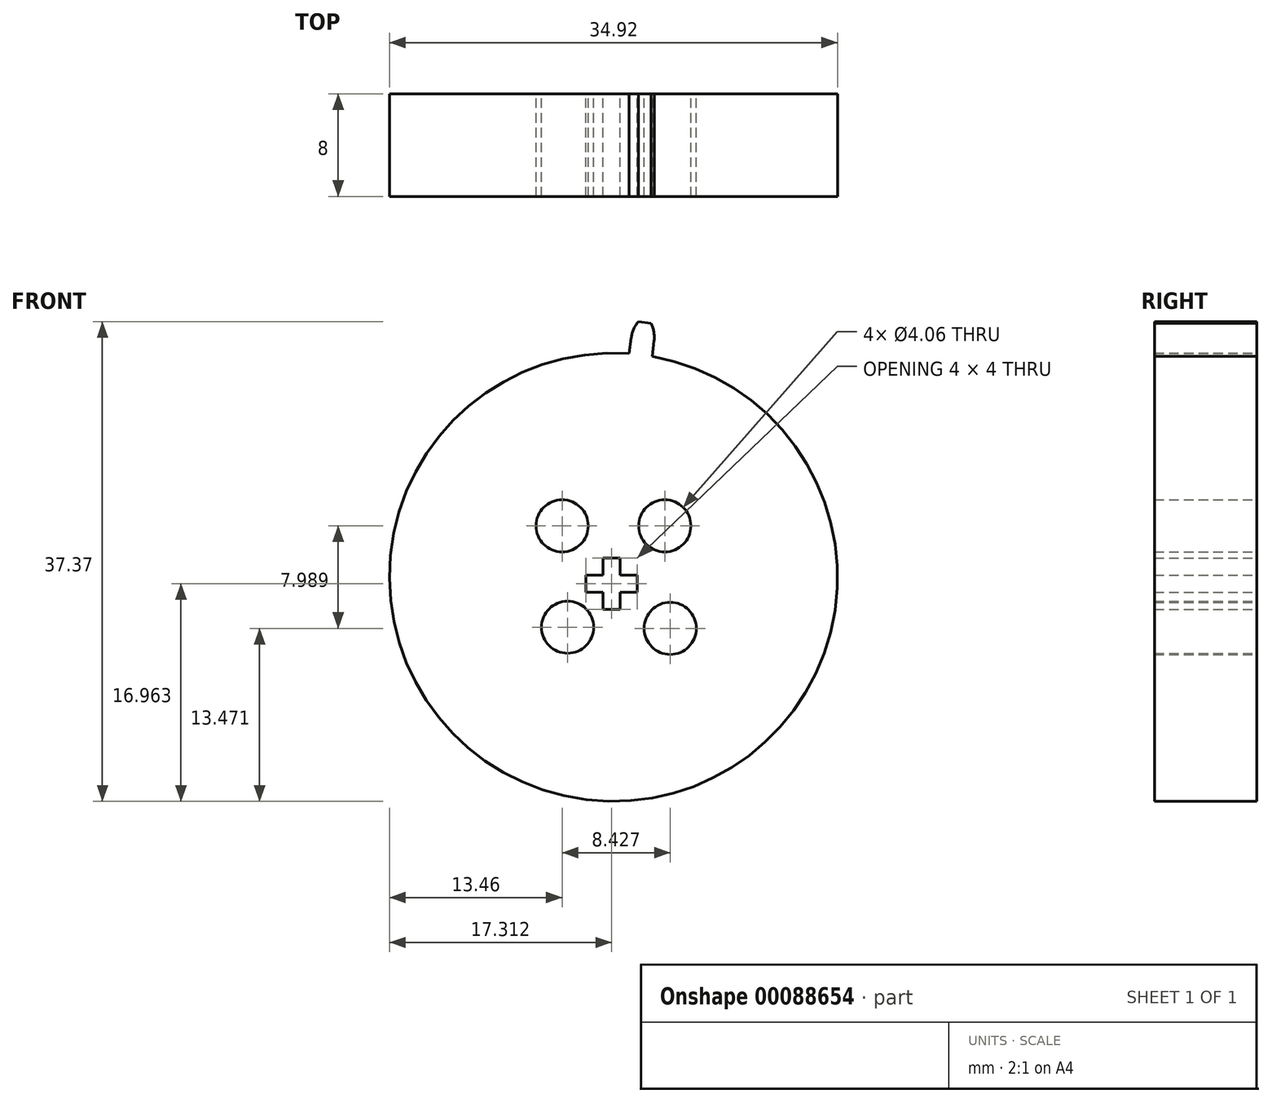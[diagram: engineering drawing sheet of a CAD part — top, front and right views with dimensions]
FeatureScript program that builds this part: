
annotation { "Feature Type Name" : "Feature", "Feature Type Description" : "" }
export const myFeature = defineFeature(function(context is Context, id is Id, definition is map)
    precondition{}
    {
        {
            var Q0;
            Q0=qCreatedBy(makeId("Front.planeOp"),FACE);
            var sketch = newSketch(context, id + "F0", { "sketchPlane" : qUnion([Q0])});
            skLineSegment(sketch, "E0", {"start": v(1.93, 19.91) * mm, "end": v(2.94, 19.79) * mm});
            skArc(sketch, "E1", {"start": v(1.23, 17.42) * mm, "mid": v(2.13, 17.33) * mm, "end": v(3.02, 17.2) * mm});
            skLineSegment(sketch, "E2", {"start": v(1.38, 18.63) * mm, "end": v(1.23, 17.42) * mm});
            skLineSegment(sketch, "E3.MirrorCS", {"start": v(3.16, 18.4) * mm, "end": v(3.02, 17.2) * mm});
            skLineSegment(sketch, "E4", {"start": v(2.13, 17.33) * mm, "end": v(2.47, 20.14) * mm, "construction": true});
            skArc(sketch, "E5", {"start": v(1.93, 19.91) * mm, "mid": v(1.57, 19.3) * mm, "end": v(1.38, 18.63) * mm});
            skArc(sketch, "E6", {"start": v(3.16, 18.4) * mm, "mid": v(3.15, 19.11) * mm, "end": v(2.94, 19.79) * mm});
            skSolve(sketch);
        }
        {
            var Q0;
            Q0=qCreatedBy(makeId("Top.planeOp"),FACE);
            var sketch = newSketch(context, id + "F1", { "sketchPlane" : qUnion([Q0])});
            skLineSegment(sketch, "E7", {"start": v(0, 0) * mm, "end": v(0, 30.53) * mm, "construction": true});
            skLineSegment(sketch, "E8", {"start": v(0, 0) * mm, "end": v(0, -25.91) * mm, "construction": true});
            skSolve(sketch);
        }
        {
            var Q0;
            Q0=qCreatedBy(makeId("Front.planeOp"),FACE);
            var sketch = newSketch(context, id + "F2", { "sketchPlane" : qUnion([Q0])});
            skCircle(sketch, "E9", {"center": v(0, 0) * mm, "radius": 17.46 * mm});
            skCircle(sketch, "E10", {"center": v(-4, 4) * mm, "radius": 2.03 * mm});
            skCircle(sketch, "E11.1.0.0", {"center": v(4, 4) * mm, "radius": 2.03 * mm});
            skLineSegment(sketch, "E11.direction1", {"start": v(-4, 4) * mm, "end": v(4, 4) * mm, "construction": true});
            skCircle(sketch, "E12.0.1.0", {"center": v(4.43, -3.99) * mm, "radius": 2.03 * mm});
            skLineSegment(sketch, "E12.direction1", {"start": v(4, 4) * mm, "end": v(23.14, 4) * mm, "construction": true});
            skLineSegment(sketch, "E12.direction2", {"start": v(4, 4) * mm, "end": v(4.43, -3.99) * mm, "construction": true});
            skCircle(sketch, "E13.1.0.0", {"center": v(-3.57, -3.9) * mm, "radius": 2.03 * mm});
            skLineSegment(sketch, "E13.direction1", {"start": v(4.43, -3.99) * mm, "end": v(-3.57, -3.9) * mm, "construction": true});
            skSolve(sketch);
        }
        {
            var Q0;
            Q0=makeQuery(id+"F2.imprint","IMPRINT",FACE,{"disambiguationData":[TD([[makeQuery(id+"F2.imprint","IMPRINT",EDGE,{"derivedFrom":sQuery(id+"F2.wireOp",EDGE,"E9")}),1.0]])]});
            extrude(context, id + "F3", {"entities" : qUnion([Q0]), "depth" : 8 * mm});
        }
        {
            var Q0;
            Q0=makeQuery(id+"F0.imprint","IMPRINT",FACE,{"disambiguationData":[TD([[makeQuery(id+"F0.imprint","IMPRINT",EDGE,{"derivedFrom":sQuery(id+"F0.wireOp",EDGE,"E0")}),-1.0]])]});
            var Q1;
            Q1=makeQuery(id+"F3.opExtrude","CAP_FACE",FACE,{"disambiguationData":[OSD([sQuery(id+"F2.wireOp",EDGE,"E9"),sQuery(id+"F2.wireOp",EDGE,"E10"),sQuery(id+"F2.wireOp",EDGE,"E11.1.0.0"),sQuery(id+"F2.wireOp",EDGE,"E12.0.1.0"),sQuery(id+"F2.wireOp",EDGE,"E13.1.0.0")])],"isStart":false});
            extrude(context, id + "F4", {"entities" : qUnion([Q0]), "operationType" : NewBodyOperationType.ADD, "endBound" : BoundingType.UP_TO_SURFACE, "endBoundEntityFace" : qUnion([Q1]), "depth" : 25.4 * mm});
        }
        {
            var Q0;
            Q0=qCreatedBy(makeId("Front.planeOp"),FACE);
            var sketch = newSketch(context, id + "F5", { "sketchPlane" : qUnion([Q0])});
            skLineSegment(sketch, "E14", {"start": v(-0.15, 3.5) * mm, "end": v(-0.15, -4.5) * mm, "construction": true});
            skLineSegment(sketch, "E15", {"start": v(0.52, 1.5) * mm, "end": v(0.52, 0.17) * mm});
            skLineSegment(sketch, "E16", {"start": v(0.52, 0.17) * mm, "end": v(1.85, 0.17) * mm});
            skLineSegment(sketch, "E17", {"start": v(1.85, 0.17) * mm, "end": v(1.85, -0.5) * mm});
            skLineSegment(sketch, "E18", {"start": v(0.52, 1.5) * mm, "end": v(-0.15, 1.5) * mm});
            skLineSegment(sketch, "E19", {"start": v(3.85, -0.5) * mm, "end": v(-2.03, -0.5) * mm, "construction": true});
            skArc(sketch, "E20.0", {"start": v(1.23, 17.42) * mm, "mid": v(-0.15, 17.46) * mm, "end": v(-1.53, 17.4) * mm});
            skArc(sketch, "E21.0", {"start": v(17.42, -1.23) * mm, "mid": v(17.46, 0.15) * mm, "end": v(17.4, 1.53) * mm, "construction": true});
            skLineSegment(sketch, "E22", {"start": v(-0.15, 17.46) * mm, "end": v(-0.15, 15.09) * mm, "construction": true});
            skLineSegment(sketch, "E23", {"start": v(17.46, 0.15) * mm, "end": v(14.56, 0.15) * mm, "construction": true});
            skLineSegment(sketch, "E24.MirrorCS", {"start": v(1.85, -1.16) * mm, "end": v(1.85, -0.5) * mm});
            skLineSegment(sketch, "E25.MirrorCS", {"start": v(0.52, -1.16) * mm, "end": v(1.85, -1.16) * mm});
            skLineSegment(sketch, "E26.MirrorCS", {"start": v(0.52, -2.5) * mm, "end": v(0.52, -1.16) * mm});
            skLineSegment(sketch, "E27.MirrorCS", {"start": v(0.52, -2.5) * mm, "end": v(-0.15, -2.5) * mm});
            skLineSegment(sketch, "E28.MirrorCS", {"start": v(-0.82, 1.5) * mm, "end": v(-0.15, 1.5) * mm});
            skLineSegment(sketch, "E29.MirrorCS", {"start": v(-0.82, 1.5) * mm, "end": v(-0.82, 0.17) * mm});
            skLineSegment(sketch, "E30.MirrorCS", {"start": v(-0.82, 0.17) * mm, "end": v(-2.15, 0.17) * mm});
            skLineSegment(sketch, "E31.MirrorCS", {"start": v(-2.15, 0.17) * mm, "end": v(-2.15, -0.5) * mm});
            skLineSegment(sketch, "E32.MirrorCS", {"start": v(-2.15, -1.16) * mm, "end": v(-2.15, -0.5) * mm});
            skLineSegment(sketch, "E33.MirrorCS", {"start": v(-0.82, -1.16) * mm, "end": v(-2.15, -1.16) * mm});
            skLineSegment(sketch, "E34.MirrorCS", {"start": v(-0.82, -2.5) * mm, "end": v(-0.82, -1.16) * mm});
            skLineSegment(sketch, "E35.MirrorCS", {"start": v(-0.82, -2.5) * mm, "end": v(-0.15, -2.5) * mm});
            skSolve(sketch);
        }
        {
            var Q0;
            Q0=qSketchRegion(id+"F5",true);
            extrude(context, id + "F6", {"entities" : qUnion([Q0]), "operationType" : NewBodyOperationType.REMOVE, "depth" : 25.4 * mm});
        }
    });
